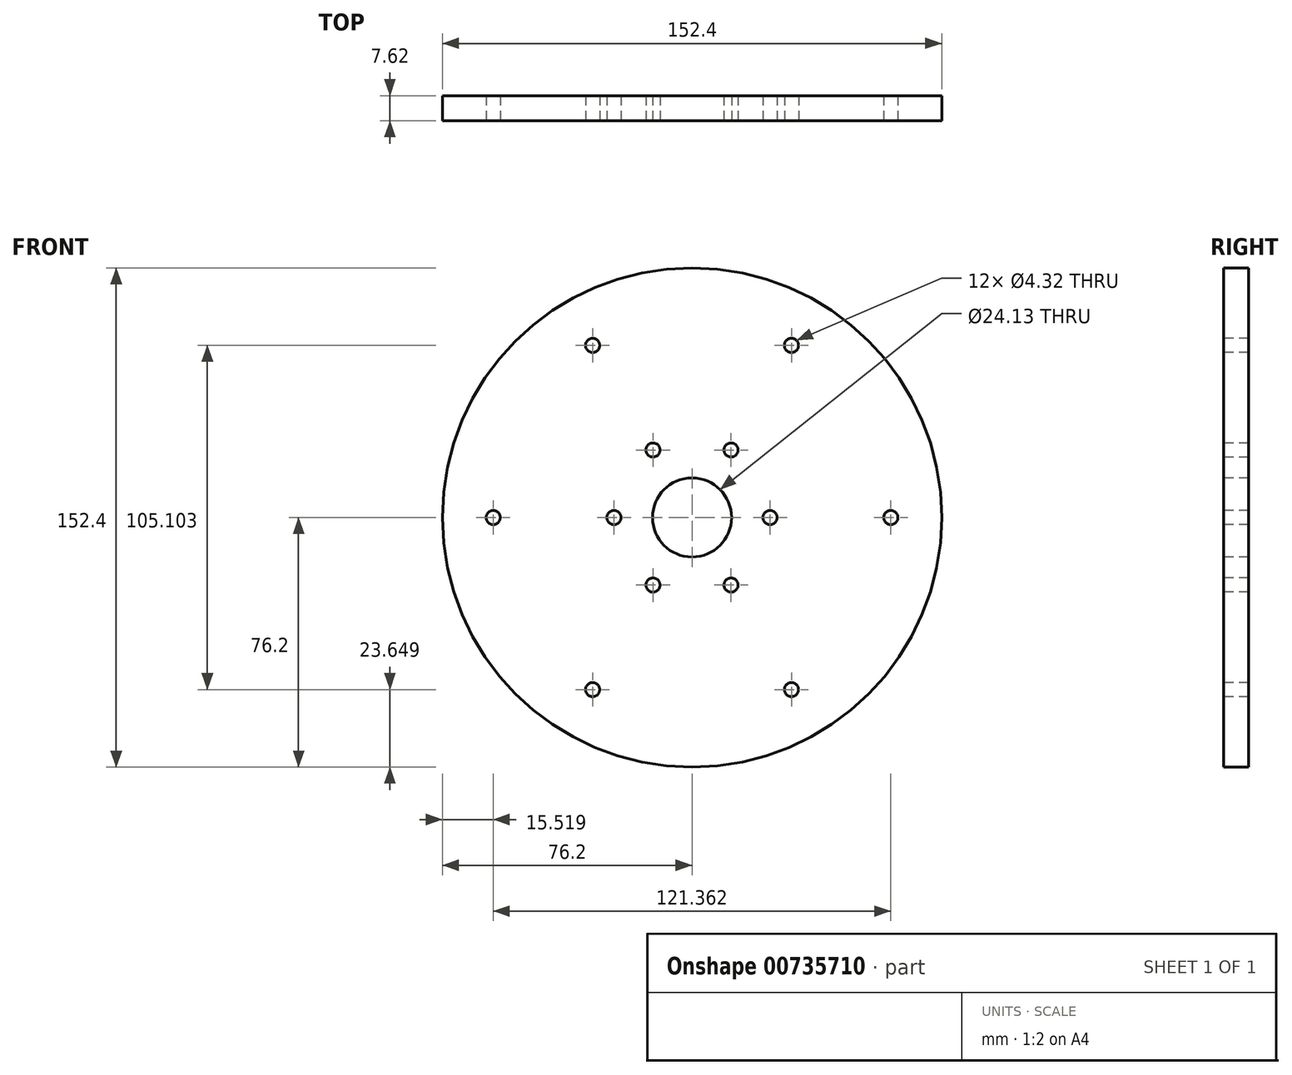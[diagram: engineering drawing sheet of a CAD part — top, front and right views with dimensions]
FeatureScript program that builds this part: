
annotation { "Feature Type Name" : "Feature", "Feature Type Description" : "" }
export const myFeature = defineFeature(function(context is Context, id is Id, definition is map)
    precondition{}
    {
        {
            var Q0;
            Q0=qCreatedBy(makeId("Front.planeOp"),FACE);
            var sketch = newSketch(context, id + "F0", { "sketchPlane" : qUnion([Q0])});
            skCircle(sketch, "E0", {"center": v(0, 0) * mm, "radius": 12.07 * mm});
            skCircle(sketch, "E1", {"center": v(0, 0) * mm, "radius": 76.2 * mm});
            skCircle(sketch, "E2.1.0", {"center": v(-60.68, 0) * mm, "radius": 2.16 * mm});
            skCircle(sketch, "E3.MirrorC", {"center": v(-23.81, 0) * mm, "radius": 2.16 * mm});
            skCircle(sketch, "E4.1.0", {"center": v(-11.9, -20.62) * mm, "radius": 2.16 * mm});
            skCircle(sketch, "E4.2.0", {"center": v(11.9, -20.62) * mm, "radius": 2.16 * mm});
            skCircle(sketch, "E4.3.0", {"center": v(23.81, 0) * mm, "radius": 2.16 * mm});
            skCircle(sketch, "E4.4.0", {"center": v(11.9, 20.62) * mm, "radius": 2.16 * mm});
            skCircle(sketch, "E4.5.0", {"center": v(-11.9, 20.62) * mm, "radius": 2.16 * mm});
            skCircle(sketch, "E5.1.0", {"center": v(-30.34, -52.55) * mm, "radius": 2.16 * mm});
            skCircle(sketch, "E5.2.0", {"center": v(30.34, -52.55) * mm, "radius": 2.16 * mm});
            skCircle(sketch, "E5.3.0", {"center": v(60.68, 0) * mm, "radius": 2.16 * mm});
            skCircle(sketch, "E5.4.0", {"center": v(30.34, 52.55) * mm, "radius": 2.16 * mm});
            skCircle(sketch, "E5.5.0", {"center": v(-30.34, 52.55) * mm, "radius": 2.16 * mm});
            skSolve(sketch);
        }
        {
            var Q0;
            Q0=makeQuery(id+"F0.imprint","IMPRINT",FACE,{"disambiguationData":[TD([[makeQuery(id+"F0.imprint","IMPRINT",EDGE,{"derivedFrom":sQuery(id+"F0.wireOp",EDGE,"E0")}),-1.0]])]});
            extrude(context, id + "F1", {"entities" : qUnion([Q0]), "oppositeDirection" : true, "depth" : 7.62 * mm, "offsetDistance" : 25.4 * mm});
        }
    });
